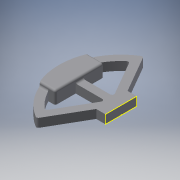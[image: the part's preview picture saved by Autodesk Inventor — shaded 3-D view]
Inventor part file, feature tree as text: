
AUTODESK INVENTOR PART (.ipt)
format: ipt  version: 2019 (Build 230136000, 136)  size: 220,160 bytes
history: native  units: mm
features: sketch x4, other x4, extrude x3, fillet x1, projected_geometry x1
ambient origin geometry x8: Origin, YZ Plane, XZ Plane, XY Plane, X Axis, Y Axis, Z Axis, Center Point
bodies: Solide1 (feature_tree)
feature tree (13):
  extrude  "Extrusion1"  Depth=160.0mm
  extrude  "Extrusion2"  TaperAngle=60.0deg  [1 undecoded]
  fillet  "Congé1"  [1 undecoded]
  extrude  "Extrusion3"  Depth=12.0mm
  sketch  "Esquisse4"
  sketch  "Esquisse1"
  sketch  "Esquisse2"
  sketch  "Esquisse3"
  projected_geometry  "Boucle projetée1"
  other  "Référence1"
  parser-record x1  (decoder bookkeeping rows leaked as tree rows — omitted from the tree; the rows remain in map.json)
  other  "ensembleFinal.iam"
  other  "planche:1"
note: 2 required parameter values undecoded (feature->parameter linkage not recoverable at this tier; creation-order binding heuristic only, values carry confidence <= 0.55)
note: 1 file-system path scrubbed to <path> (originals preserved in map.json)
